# Revit family: Gleitlager T HV3, m.D., Ø64 bis Ø219mm (h=151mm bis 177mm)
name_source: partatom
category: HLS-Bauteile
revit_build: Autodesk Revit 2018 (Build: 20190510_1515(x64)
units: mm (PartAtom-declared; Revit-internal decimal feet)

## family parameters
Arbeitsebenenbasiert = Ja
Beim Laden mit Abzugskörper schneiden = Nein
Bemaßung runder Anschluss = Durchmesser verwenden
Gemeinsam genutzt = Ja
Immer vertikal = Nein
Klassifizierung = Keine
Raumberechnungspunkt = Nein
Teiletyp = Normal

## types (13) — shared parameters
Anzahl Rohrschellen = 2
Baustoffklasse = B2
Breite Schellenband = 50 mm
Breite Unterbau = 100 mm
Dämmstärke = 6 mm  [stored 0.019685 ft]
Fabrikat = MEFA
Hersteller = MEFA
Kurztext1 = Gleitlager T 2 RS HV3 50x5
Länge Unterbau = 250 mm
Mengeneinheit = St
Schalldämmeinlage = Gummi EPDM
Sicherheitsfaktor = 1.54
Stärke Material = 8 mm  [stored 0.0262467 ft]
Stärke Schellenband = 5 mm
Verschluss = Mutter / Verschluss-Schraube
Vorgabe-Ansicht = 1219 mm
max. Höhe Unterbau = 175 mm
max. Temperaturbeständigkeit = 100 °C
min. Höhe Unterbau = 150 mm
vpe = 1
zero-valued in all types: max. Rohraußendurchmesser, min. Rohraußendurchmesser

## per-type parameters (varying)
| type | Artikelnummer | EAN | Gewicht | Gewicht pro Bauteil | Kurztext2 | Schellenteil | max. Rohrachse | min. Rohrachse |
| Typ HV3, m. 2 RS, m.D., Ø64mm (h=151 bis 177mm) | 141cfbb0064 | 4250928461445 | 5.56 kg | 5.56 kg | 64 mm EPDM 100x250 mm fsv | TL-141S_b0076 bis 0231, m.D : mit RS Ø64mm m.D | 209 mm | 183 mm |
| Typ HV3, m. 2 RS, m.D., Ø76mm (h=151 bis 177mm) | 141cfbb0076 | 4250928461452 | 5.77 kg | 5.77 kg | 76 mm EPDM 100x250 mm fsv | TL-141S_b0076 bis 0231, m.D : mit RS Ø76mm m.D | 215 mm | 189 mm |
| Typ HV3, m. 2 RS, m.D., Ø89mm (h=151 bis 177mm) | 141cfbb0089 | 4250928461469 | 5.97 kg | 5.97 kg | 89 mm EPDM 100x250 mm fsv | TL-141S_b0076 bis 0231, m.D : mit RS Ø88.9mm, m.D | 222 mm | 196 mm |
| Typ HV3, m. 2 RS, m.D., Ø108mm (h=151 bis 177mm) | 141cfbb0108 | 4250928461476 | 6.27 kg | 6.27 kg | 108 mm EPDM 100x250 mm fsv | TL-141S_b0076 bis 0231, m.D : mit RS Ø108mm m.D | 231 mm | 205 mm |
| Typ HV3, m. 2 RS, m.D., Ø110mm (h=151 bis 177mm) | 141cfbb0110 | 4250928461483 | 6.30 kg | 6.30 kg | 110 mm EPDM 100x250 mm fsv | TL-141S_b0076 bis 0231, m.D : mit RS Ø110mm m.D | 232 mm | 206 mm |
| Typ HV3, m. 2 RS, m.D., Ø114mm (h=151 bis 177mm) | 141cfbb0114 | 4250928461490 | 6.37 kg | 6.37 kg | 114 mm EPDM 100x250 mm fsv | TL-141S_b0076 bis 0231, m.D : mit RS Ø114.3mm m.D | 234 mm | 208 mm |
| Typ HV3, m. 2 RS, m.D., Ø133mm (h=151 bis 177mm) | 141cfbb0133 | 4250928461506 | 6.67 kg | 6.67 kg | 133 mm EPDM 100x250 mm fsv | TL-141S_b0076 bis 0231, m.D : mit RS Ø133mm m.D | 244 mm | 218 mm |
| Typ HV3, m. 2 RS, m.D., Ø140mm (h=151 bis 177mm) | 141cfbb0140 | 4250928461513 | 6.79 kg | 6.79 kg | 140 mm EPDM 100x250 mm fsv | TL-141S_b0076 bis 0231, m.D : mit RS Ø139.7mm m.D | 247 mm | 221 mm |
| Typ HV3, m. 2 RS, m.D., Ø160mm (h=151 bis 177mm) | 141cfbb0160 | 4250928461520 | 7.11 kg | 7.11 kg | 160 mm EPDM 100x250 mm fsv | TL-141S_b0076 bis 0231, m.D : mit RS Ø160mm m.D | 257 mm | 231 mm |
| Typ HV3, m. 2 RS, m.D., Ø168mm (h=151 bis 177mm) | 141cfbb0168 | 4250928461537 | 7.24 kg | 7.24 kg | 168 mm EPDM 100x250 mm fsv | TL-141S_b0076 bis 0231, m.D : mit RS Ø168.3mm m.D | 261 mm | 235 mm |
| Typ HV3, m. 2 RS, m.D., Ø180mm (h=151 bis 177mm) | 141cfbb0180 | 4250928461544 | 7.43 kg | 7.43 kg | 180 mm EPDM 100x250 mm fsv | TL-141S_b0076 bis 0231, m.D : mit RS Ø180mm m.D | 267 mm | 241 mm |
| Typ HV3, m. 2 RS, m.D., Ø210mm (h=151 bis 177mm) | 141cfbb0210 | 4250928461551 | 7.91 kg | 7.91 kg | 210 mm EPDM 100x250 mm fsv | TL-141S_b0076 bis 0231, m.D : mit RS Ø210mm m.D | 282 mm | 256 mm |
| Typ HV3, m. 2 RS, m.D., Ø219mm (h=151 bis 177mm) | 141cfbb0219 | 4250928461568 | 8.05 kg | 8.05 kg | 219 mm EPDM 100x250 mm fsv | TL-141S_b0076 bis 0231, m.D : mit RS Ø219mm m.D | 287 mm | 261 mm |

note: [stored X ft] marks values corroborated as IEEE doubles in the binary element streams (Revit-internal decimal feet)

## geometry (parser evidence)
native form markers: Sweep x8
no freeform markers — native parametric forms only
